# Revit family: CENTUM Wandanschluß
name_source: partatom
category: HLS-Bauteile
revit_build: Autodesk Revit 2017 (Build: 20190507_1515(x64)
units: mm (PartAtom-declared; Revit-internal decimal feet)

## family parameters
Arbeitsebenenbasiert = Ja
Beim Laden mit Abzugskörper schneiden = Nein
Bemaßung runder Anschluss = Durchmesser verwenden
Gemeinsam genutzt = Ja
Immer vertikal = Nein
Raumberechnungspunkt = Nein
Teiletyp = Normal

## types (2) — shared parameters
Fabrikat = MEFA
Firma = MEFA Befestigungs- und Montagesysteme GmbH
Kurztext2 = Platte 160x55x12 mm
Material = Stahl
Mengeneinheit = St
Vorgabe-Ansicht = 1219 mm
vpe = 1 St

## per-type parameters (varying)
| type | Artikelnummer | C | EAN | Gewicht | Gewicht pro Bauteil | Kurztext1 | Platte 80x |
| CENTUM Wandanschluß M12 | 1620004010 | 5 mm  [stored 0.0164042 ft] | 4250928449658 | 1.18 kg | 1.18 kg | Wandanschluss M12 | Platte  80x .... : Platte  80x 50x10 14 |
| CENTUM Wandanschluß M16 | 1620004011 | 6 mm  [stored 0.019685 ft] | 4250928449665 | 1.28 kg | 1.28 kg | Wandanschluss M16 | Platte  80x .... : Platte  80x 55x12 17 |

note: [stored X ft] marks values corroborated as IEEE doubles in the binary element streams (Revit-internal decimal feet)
